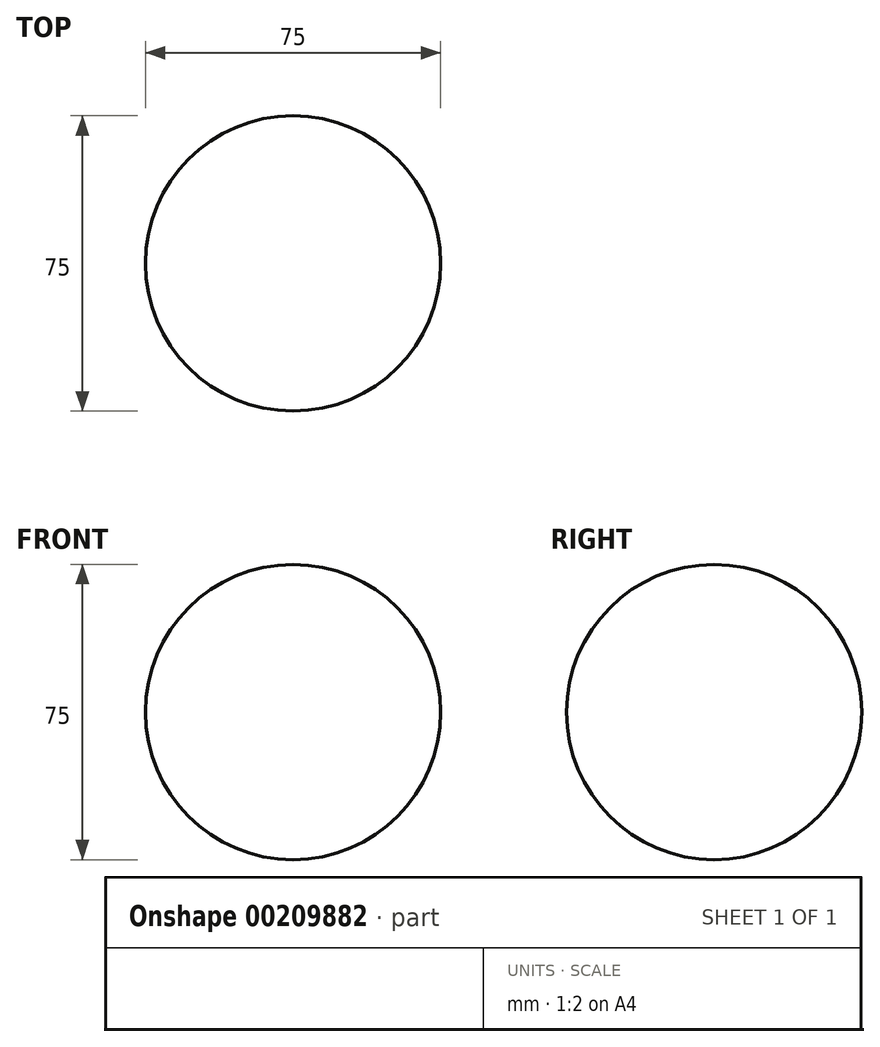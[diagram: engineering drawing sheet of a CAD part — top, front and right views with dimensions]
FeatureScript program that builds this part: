
annotation { "Feature Type Name" : "Feature", "Feature Type Description" : "" }
export const myFeature = defineFeature(function(context is Context, id is Id, definition is map)
    precondition{}
    {
        {
            var Q0;
            Q0=qCreatedBy(makeId("Top.planeOp"),FACE);
            var sketch = newSketch(context, id + "F0", { "sketchPlane" : qUnion([Q0])});
            skCircle(sketch, "E0", {"center": v(0, 0) * mm, "radius": 37.5 * mm});
            skSolve(sketch);
        }
        {
            var Q0;
            Q0=makeQuery(id+"F0.imprint","IMPRINT",FACE,{"disambiguationData":[TD([[makeQuery(id+"F0.imprint","IMPRINT",EDGE,{"derivedFrom":sQuery(id+"F0.wireOp",EDGE,"E0")}),1.0]])]});
            extrude(context, id + "F1", {"entities" : qUnion([Q0]), "endBound" : BoundingType.SYMMETRIC, "depth" : 75 * mm});
        }
        {
            var Q0;
            Q0=makeQuery(id+"F1.opExtrude","CAP_FACE",FACE,{"disambiguationData":[OSD([sQuery(id+"F0.wireOp",EDGE,"E0")])],"isStart":false});
            var Q1;
            Q1=makeQuery(id+"F1.opExtrude","CAP_FACE",FACE,{"disambiguationData":[OSD([sQuery(id+"F0.wireOp",EDGE,"E0")])],"isStart":true});
            fillet(context, id + "F2", {"entities" : qUnion([Q0, Q1]), "radius" : 37.5 * mm, "tangentPropagation" : true, "allowEdgeOverflow" : false});
        }
    });
